# Revit family: 3031850 Lighting Fixture_Sylvania_Syl-Lighter II_Ceiling Recessed
name_source: partatom
category: Lighting Fixtures
revit_build: Autodesk Revit 2017 (Build: 20190507_1515(x64)
units: mm (PartAtom-declared; Revit-internal decimal feet)

## family parameters
Cut with Voids When Loaded = No
Host = Face
Light Source = Yes
OmniClass Number = 23.80.70.11.17
OmniClass Title = Specialized Lighting by Location or Use
Part Type = Normal
Room Calculation Point = No
Round Connector Dimension = Use Diameter
Shared = No

## types (1)
- Syl-Lighter LED II 165 RO 12W NW 1-10V
    Accessory Diameter = 165 mm
    Accessory Material = Aluminum_Sylvania_Syl-Lighter LED II_White_RAL 9003
    Accessory Radius = 82.5 mm
    Apparent Load = 14 VA
    Assembly Code = D5020200
    Beam Angle = 74.00°
    Body Material = Metal_Sylvania_Syl-Lighter LED II_Silver
    Catalog Number = 3031850 Syl-Lighter LED II 165 RO 14W NW 1-10V
    Color Filter = 16777215
    Cutout Diameter = 145 mm  [stored 0.475722 ft]
    Default Elevation = 0 mm  [stored 0 ft]
    Description = Ceiling recessed IP44 LED downlight, perfect where limited ceiling void is available with only 45mm product depth and 145mm cutout. Ideal replacement for 1x26W CFL downlights. The polycarbonate diffuser allows for a wider light distribution and increased spacings between luminiares. Loop in loop out connector allows for quick installation. Die-cast aluminium body, 1186LM, 14W, 85lm/W, 4000K, Driver Current: 300mA, CRI80, 74° beam angle, 1-10V dimmable LED driver, IP44, IK07, 50,000 hrs (L70), (HxW) 45x165mm, 5 step MacAdam ellipse, 0.38kg, RAL9003, Class 2, 220-240V, energy class: A++, A+, A
    Diameter = 145 mm  [stored 0.475722 ft]
    Diffuser Diameter = 125 mm
    Diffuser Material = Polycarbonate_Sylvania_Syl-Lighter LED II_Opal
    Diffuser Radius = 62.5 mm
    Dimmable = DALI
    Dimming Lamp Color Temperature Shift = <None>
    Drive Current = 300mA
    Electrical Protection = CLASS II
    Emit Shape Visible in Rendering = No
    Emit from Circle Diameter = 125 mm
    Energy Class = A++, A+, A
    Glow Wire Test = 650 °C
    Height = 45 mm  [stored 0.147638 ft]
    IK Rating = IK07
    IP Rating = IP44
    Inner Diameter = 141 mm  [stored 0.462598 ft]
    Lamp = LED
    Lamp Comments = Integrated LED
    Life = 50 000h
    Manufacturer = Feilo Sylvania
    Model = Syl-Lighter LED II 165 RO 14W NW 1-10V
    Photometric Web File = 3031850.ies
    Product Family = SYL-LIGHTER LED II
    Product Page URL = http://www.sylvania-lighting.com
    Recessed Depth = 45 mm  [stored 0.147638 ft]
    Ta Rating = -10°C to +40°C
    Tilt Angle = -90.00°
    URL = http://www.sylvania-lighting.com
    Voltage = 240 V
    Voltage Comments = UNV (Universal Voltage; 220-240 Volt)
    Weight = 0.45 kg

note: [stored X ft] marks values corroborated as IEEE doubles in the binary element streams (Revit-internal decimal feet)

## geometry (parser evidence)
native form markers: Blend x4, Sweep x2
no freeform markers — native parametric forms only
